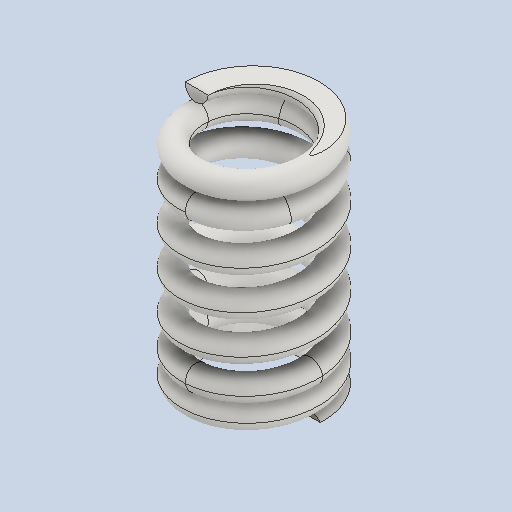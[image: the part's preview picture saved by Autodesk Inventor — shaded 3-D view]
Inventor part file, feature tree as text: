
AUTODESK INVENTOR PART (.ipt)
format: ipt  version: 2022 (Build 260153000, 153)  size: 1,047,040 bytes
history: native  units: mm
features: other x41, sketch x31, extrude x8, helix x4, sweep x2
ambient origin geometry x8: Origin, YZ Plane, XZ Plane, XY Plane, X Axis, Y Axis, Z Axis, Center Point
bodies: Solid1 (feature_tree)
feature tree (86):
  other  "Caminho helicoidal principal (direita)"
  other  "Plano de trabalho de seção (direita)"
  other  "Plano de trabalho inicial (direita)"
  other  "Plano de trabalho final (direita)"
  other  "Plano de trabalho de corte final (direita)"
  other  "Plano de trabalho de corte inicial (direita)"
  other  "Plano de trabalho de corte final normal 1 (direita)"
  other  "Plano de trabalho de corte final normal 2 (direita)"
  sweep  "Main Coil Feature(R)"
  other  "Espiral de transição inicial 1 (direita)"
  helix  "Coil  Start Transition 2(R)"  [1 undecoded]
  helix  "Coil  Start Transition 3(R)"  [1 undecoded]
  helix  "Coil  Start Transition 4(R)"  [1 undecoded]
  other  "Espiral de extremidades iniciais (direita)"
  extrude  "Operação de corte inicial (direita)"  Depth=10.0mm
  other  "Espiral de transição final 1 (direita)"
  other  "Espiral de transição final 2 (direita)"
  other  "Espiral de transição final 3 (direita)"
  other  "Espiral de transição final 4 (direita)"
  other  "Espiral final (direita)"
  extrude  "Operação de corte final (direita)"  Depth=10.0mm
  extrude  "Operação de corte de extremidades normais 1 (direita)"  Depth=6.0mm
  extrude  "Plain Ends Cut  2(R)"  Depth=6.0mm
  other  "Caminho helicoidal principal (esquerda)"
  other  "Plano de trabalho de seção (esquerda)"
  other  "Plano de trabalho inicial (esquerda)"
  other  "Plano de trabalho final (esquerda)"
  other  "Plano de trabalho de corte final (esquerda)"
  other  "Plano de trabalho de corte inicial (esquerda)"
  other  "Plano de trabalho de corte de extremidades normais 1 (esquerda)"
  other  "Plano de trabalho de corte de extremidades normais 2 (esquerda)"
  sweep  "Main Coil Feature(L)"
  other  "Espiral de transição inicial 1 (esquerda)"
  other  "Espiral de transição inicial 2 (esquerda)"
  other  "Espiral de transição inicial 3 (esquerda)"
  other  "Espiral de transição inicial 4 (esquerda)"
  other  "Espiral de extremidades iniciais (esquerda)"
  extrude  "Operação de corte inicial (esquerda)"  TaperAngle=0.0deg  [1 undecoded]
  helix  "Coil End Transition 1(L)"  [1 undecoded]
  other  "Espiral de transição final 2 (esquerda)"
  other  "Espiral de transição final 3 (esquerda)"
  other  "Espiral de transição final 4 (esquerda)"
  other  "Espiral final (esquerda)"
  extrude  "Operação de corte final (esquerda)"  Depth=0.25mm
  extrude  "Cut Plain Ends Cut 1(L)"  Depth=10.0mm
  extrude  "Cut Plain Ends Cut 2(L)"  Depth=1.942655mm
  other  "Plano de trabalho baseado em iMate"
  other  "Visualização do centro"
  other  "Vissualiação do eixo X"
  sketch  "Esboço de corte de caminho (direita)"  dims[d0=0.25mm d2=1.684938mm d3=10.0mm d4=32.5mm]
  other  "Srf1"
  sketch  "Esboço de corte helicoidal (direita)"  dims[d5=0.0mm d6=90.0deg d7=90.0deg d8=0.0mm d9=0.0mm d12=1.942655mm d13=-2.508302mm d14=1.0mm]
  sketch  "Esboço helicoidal de transição inicial 1 (direita)"  dims[d15=0.0mm]
  sketch  "Sketch  Start Transition 2(R)"  dims[d16=1.513704mm d17=10.0mm d18=2.5mm d19=0.0mm d20=90.0deg d21=90.0deg d22=0.0mm d23=0.0mm]
  sketch  "Sketch  Start Transition 3(R)"  dims[d24=1.342469mm d25=10.0mm d26=2.5mm d27=0.0mm d28=90.0deg d29=90.0deg d30=0.0mm d31=0.0mm]
  sketch  "Sketch  Start Transition 4(R)"  dims[d32=1.171235mm d33=10.0mm d34=2.5mm d35=0.0mm d36=90.0deg d37=90.0deg d38=0.0mm d39=0.0mm]
  sketch  "Esboço helicoidal de transição final 1 (direita)"  dims[d40=1.0mm d41=10.0mm d42=2.5mm d43=0.0mm d44=90.0deg d45=90.0deg d46=0.0mm d47=0.0mm]
  sketch  "Esboço helicoidal de transição final 2 (direita)"  dims[d48=1.513704mm d49=10.0mm d50=1.875mm d51=0.0mm d52=90.0deg d53=90.0deg d54=0.0mm d55=0.0mm]
  sketch  "Esboço helicoidal de transição final 3 (direita)"  dims[d56=1.342469mm d57=10.0mm d58=1.875mm d59=0.0mm d60=90.0deg d61=90.0deg d62=0.0mm d63=0.0mm]
  sketch  "Esboço helicoidal de transição final 4 (direita)"  dims[d64=1.171235mm d65=10.0mm d66=1.875mm d67=0.0mm d68=90.0deg d69=90.0deg d70=0.0mm d71=0.0mm]
  sketch  "Esboço de extremidades iniciais (direita)"  dims[d72=1.0mm d73=10.0mm d74=1.875mm d75=0.0mm d76=90.0deg d77=90.0deg d78=0.0mm d79=0.0mm d81=10.0mm d82=15.0mm]
  sketch  "Esboço helicoidal final (direita)"  dims[d83=0.0mm d84=90.0deg d85=90.0deg d86=0.0mm d87=0.0mm d88=1.005737mm d89=10.0mm d90=10.0mm]
  sketch  "Esboço de corte final (direita)"  dims[d91=0.0mm d92=90.0deg d93=90.0deg d94=0.0mm d95=0.0mm d96=6.0mm]
  sketch  "Esboço de corte inicial (direita)"  dims[d97=1.005737mm d98=0.0mm d99=6.0mm]
  sketch  "Esboço de corte de caminho (esquerda)"  dims[d100=1.005737mm d101=0.0mm]
  other  "Srf2"
  sketch  "Esboço de corte helicoidal (esquerda)"  dims[d102=0.0mm d103=0.0mm d104=0.0mm d105=0.0mm d106=0.0mm d108=0.0mm d112=0.0mm d113=0.0mm d114=0.0mm d121=0.257154mm]
  sketch  "Esboço helicoidal de transição inicial 1 (esquerda)"  dims[d131=0.0mm d132=0.0mm d133=0.0mm]
  sketch  "Esboço helicoidal de transição inicial 2 (esquerda)"  dims[d134=0.0mm d135=0.25mm]
  sketch  "Esboço helicoidal de transição inicial 3 (esquerda)"  dims[d137=1.684938mm d138=10.0mm d139=32.5mm]
  sketch  "Esboço helicoidal de transição inicial 4 (esquerda)"  dims[d140=0.0mm d141=90.0deg d142=90.0deg d143=0.0mm d144=0.0mm d145=1.942655mm]
  sketch  "Esboço de extremidades iniciais (esquerda)"  dims[d146=-2.508302mm]
  sketch  "Esboço de corte inicial (esquerda)"  dims[d147=0.257154mm]
  sketch  "Esboço helicoidal de transição final 1 (esquerda)"  dims[d148=0.00572mm]
  sketch  "Esboço helicoidal de transição final 2 (esquerda)"  dims[d149=1.0mm]
  other  "Esoço helicoidal de transição final 3 (esquerda)"
  sketch  "Esboço helicoidal de transição final 4 (esquerda)"  dims[d150=0.0mm]
  sketch  "Esboço helicoidal final (esquerda)"  dims[d151=0.0mm]
  sketch  "Esboço de corte final (esquerda)"  dims[d152=1.513704mm d153=10.0mm d154=2.5mm d155=0.0mm d156=90.0deg d157=90.0deg d158=0.0mm d159=0.0mm]
  sketch  "Esboço de corte de extremidades normais 2 (esquerda)"  dims[d160=1.342469mm]
  sketch  "Esboço de corte de extremidades normais 2 (direita)"  dims[d161=10.0mm d162=2.5mm d163=0.0mm d164=90.0deg d165=90.0deg d166=0.0mm d167=0.0mm]
  sketch  "Esboço de corte de extremidades normais 1 (direita)"  dims[d168=1.171235mm]
  sketch  "Esboço de corte de extremidades normais 1 (esquerda)"  dims[d169=10.0mm d170=2.5mm d171=0.0mm d172=90.0deg d173=90.0deg d174=0.0mm d175=0.0mm d176=1.0mm d177=10.0mm d178=2.5mm d179=0.0mm d180=90.0deg d181=90.0deg d182=0.0mm d183=0.0mm d184=10.0mm d185=10.0mm d186=10.0mm d187=10.0mm d188=1.005737mm d189=10.0mm d190=15.0mm d191=0.0mm d192=90.0deg d193=90.0deg d194=0.0mm d195=0.0mm d196=10.0mm d197=6.0mm d198=1.005737mm d199=0.0mm d200=10.0mm d201=1.513704mm d202=10.0mm d203=1.875mm d204=0.0mm d205=90.0deg d206=90.0deg d207=0.0mm d208=0.0mm d209=10.0mm d210=1.342469mm d211=10.0mm d212=1.875mm d213=0.0mm d214=90.0deg d215=90.0deg d216=0.0mm d217=0.0mm d218=1.171235mm d219=10.0mm d220=1.875mm d221=0.0mm d222=90.0deg d223=90.0deg d224=0.0mm d225=0.0mm d226=1.0mm d227=10.0mm d228=1.875mm d229=0.0mm d230=90.0deg d231=90.0deg d232=0.0mm d233=0.0mm d234=10.0mm d235=10.0mm d236=10.0mm d237=1.005737mm d238=10.0mm d239=10.0mm d240=0.0mm d241=90.0deg d242=90.0deg d243=0.0mm d244=0.0mm d245=6.0mm d246=1.005737mm d247=0.0mm d248=10.0mm d249=10.0mm d254=6.0mm d255=10.0mm d256=0.0mm d257=20.0mm d258=-0.00572mm d259=6.0mm d260=10.0mm d261=0.0mm d262=10.0mm d263=6.0mm d264=10.0mm d265=0.0mm d266=10.0mm d267=0.0mm d270=-2.383302mm d271=0.0mm d272=6.0mm d273=10.0mm d274=0.0mm d275=20.0mm d276=-157.079633mm d277=5.0mm d278=5.0mm d279=0.0mm d280=0.0mm]
  other  "Seção inicial do Plano de trabalho"
  other  "Curva básica (direita)"
  other  "Curva básica (esquerda)"
note: 5 required parameter values undecoded (feature->parameter linkage not recoverable at this tier; creation-order binding heuristic only, values carry confidence <= 0.55)
